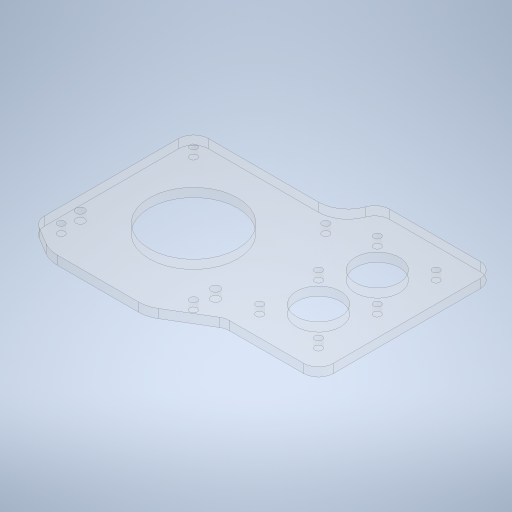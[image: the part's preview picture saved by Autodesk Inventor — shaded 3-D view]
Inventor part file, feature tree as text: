
AUTODESK INVENTOR PART (.ipt)
format: ipt  version: 2023 (Build 270158000, 158)  size: 422,912 bytes
history: native  units: in
note: dims shown in document units (in); Inventor stores cm internally (conversion verified against a paired STEP export)
features: extrude x1
ambient origin geometry x8: Origin, YZ Plane, XZ Plane, XY Plane, X Axis, Y Axis, Z Axis, Center Point
bodies: Body1 (feature_tree)
feature tree (1):
  extrude  "Extrusion2"  Depth=3.5433in
